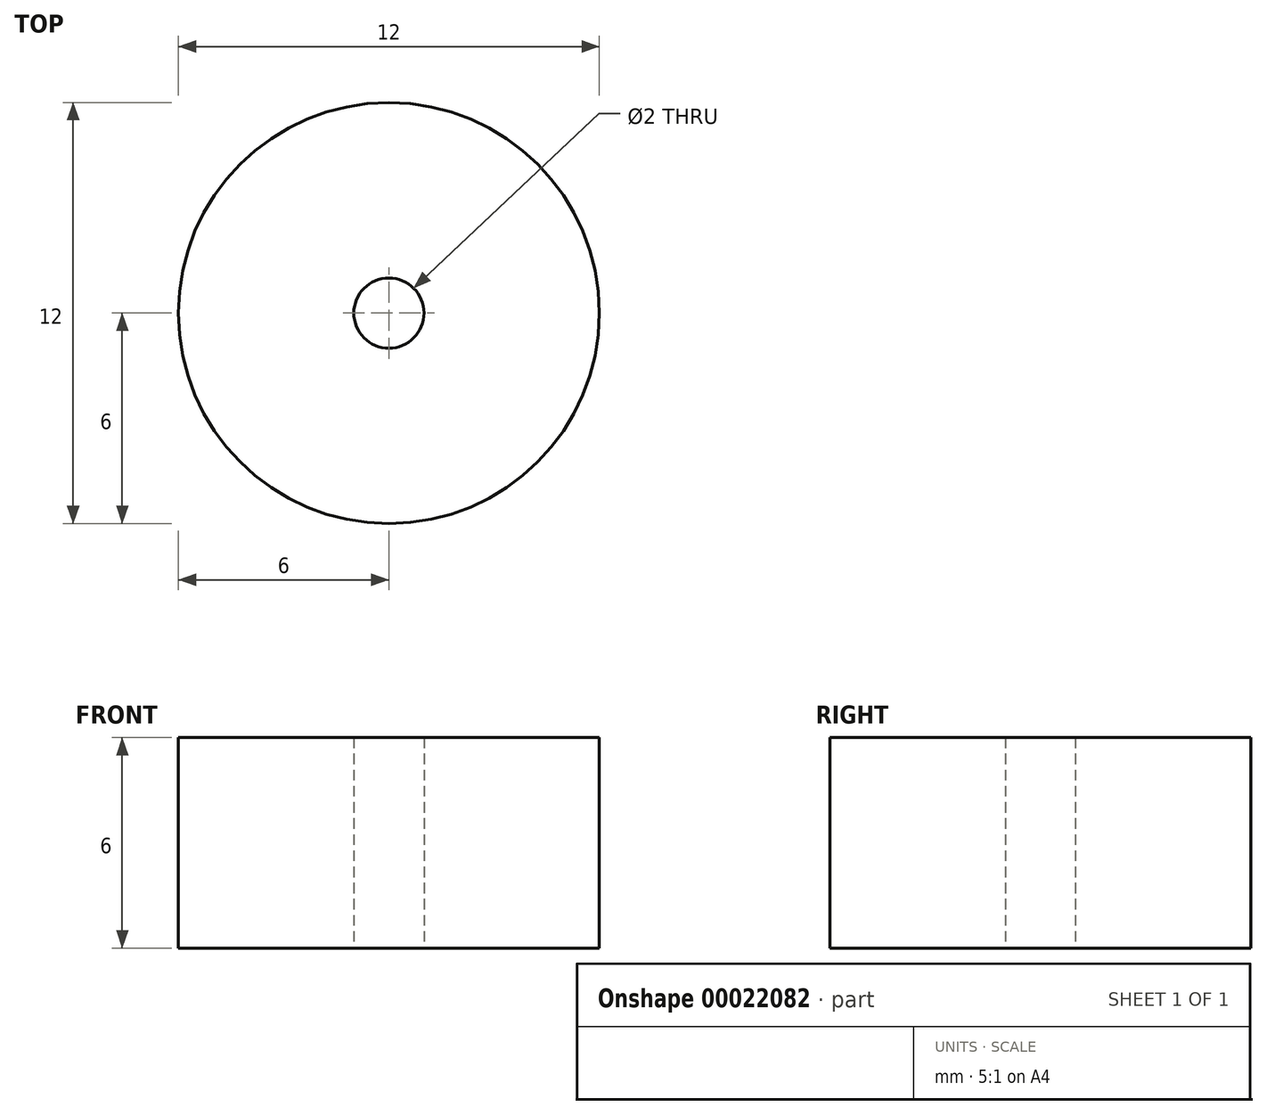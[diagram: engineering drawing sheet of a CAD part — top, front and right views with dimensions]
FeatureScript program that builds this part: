
annotation { "Feature Type Name" : "Feature", "Feature Type Description" : "" }
export const myFeature = defineFeature(function(context is Context, id is Id, definition is map)
    precondition{}
    {
        {
            var Q0;
            Q0=qCreatedBy(makeId("Top.planeOp"),FACE);
            var sketch = newSketch(context, id + "F0", { "sketchPlane" : qUnion([Q0])});
            skCircle(sketch, "E0", {"center": v(0, 0) * mm, "radius": 6 * mm});
            skPoint(sketch, "E1.orphan", {"position": v(-6, 0) * mm});
            skCircle(sketch, "E2", {"center": v(0, 0) * mm, "radius": 1 * mm});
            skSolve(sketch);
        }
        {
            var Q0;
            Q0=makeQuery(id+"F0.imprint","IMPRINT",FACE,{"disambiguationData":[TD([[makeQuery(id+"F0.imprint","IMPRINT",EDGE,{"derivedFrom":sQuery(id+"F0.wireOp",EDGE,"E0")}),1.0]])]});
            extrude(context, id + "F1", {"entities" : qUnion([Q0]), "endBound" : BoundingType.SYMMETRIC, "depth" : 6 * mm});
        }
    });
